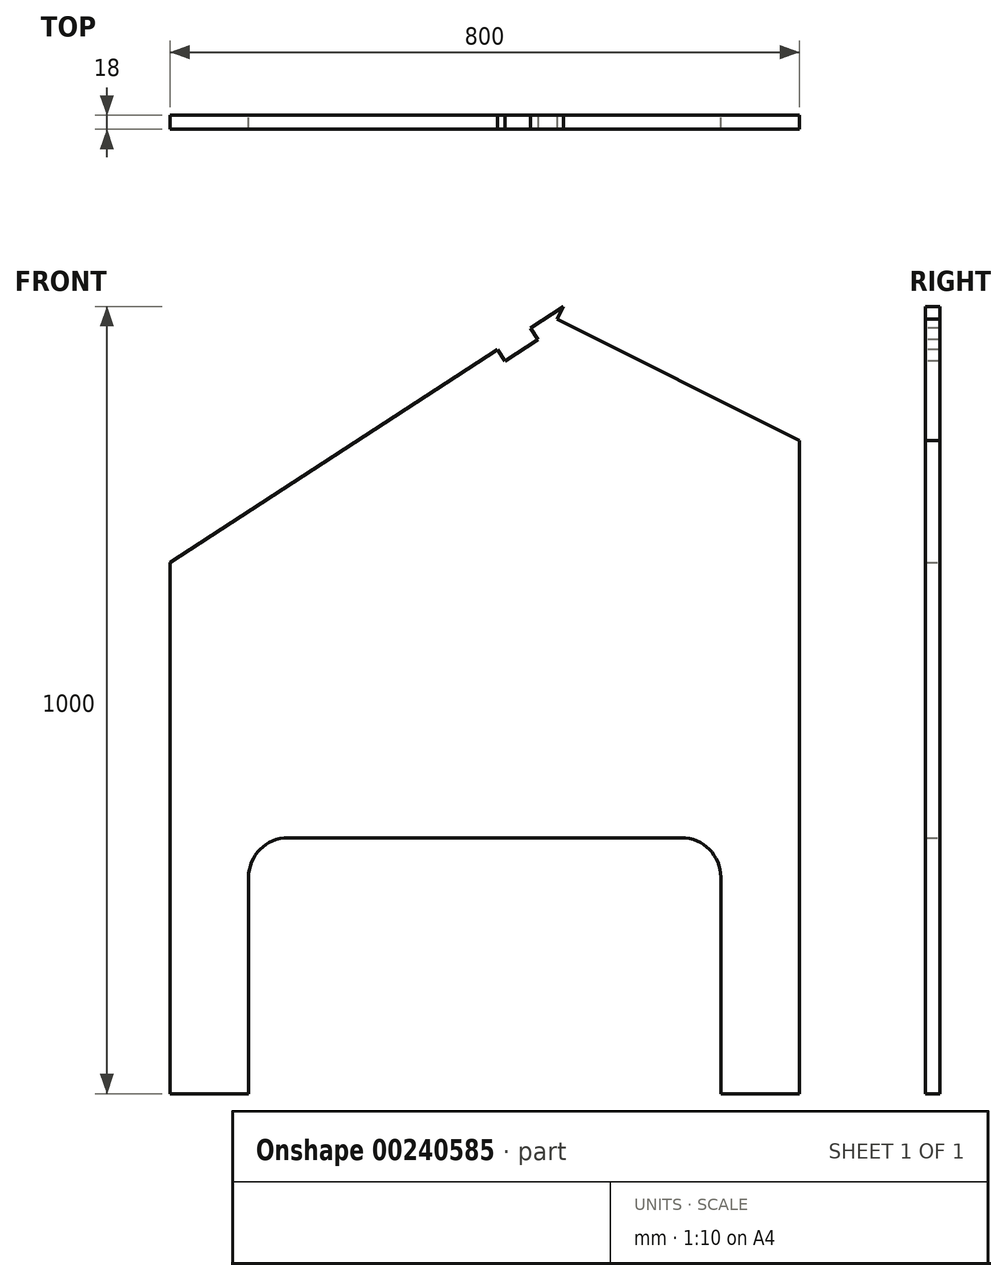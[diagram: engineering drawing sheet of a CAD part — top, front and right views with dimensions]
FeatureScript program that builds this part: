
annotation { "Feature Type Name" : "Feature", "Feature Type Description" : "" }
export const myFeature = defineFeature(function(context is Context, id is Id, definition is map)
    precondition{}
    {
        {
            var Q0;
            Q0=qCreatedBy(makeId("Front.planeOp"),FACE);
            var sketch = newSketch(context, id + "F0", { "sketchPlane" : qUnion([Q0])});
            skLineSegment(sketch, "E0.bottom", {"start": v(0, 0) * mm, "end": v(800, 0) * mm});
            skLineSegment(sketch, "E0.top", {"start": v(0, 1000) * mm, "end": v(800, 1000) * mm});
            skLineSegment(sketch, "E0.left", {"start": v(0, 0) * mm, "end": v(0, 1000) * mm});
            skLineSegment(sketch, "E0.right", {"start": v(800, 0) * mm, "end": v(800, 1000) * mm});
            skLineSegment(sketch, "E1.bottom", {"start": v(100, 0) * mm, "end": v(700, 0) * mm});
            skLineSegment(sketch, "E1.top", {"start": v(150, 325) * mm, "end": v(650, 325) * mm});
            skLineSegment(sketch, "E1.left", {"start": v(100, 0) * mm, "end": v(100, 275) * mm});
            skLineSegment(sketch, "E1.right", {"start": v(700, 0) * mm, "end": v(700, 275) * mm});
            skLineSegment(sketch, "E2", {"start": v(0, 675) * mm, "end": v(500, 1000) * mm});
            skLineSegment(sketch, "E3", {"start": v(500, 1000) * mm, "end": v(800, 850) * mm});
            skPoint(sketch, "E4.visualSharp", {"position": v(100, 325) * mm});
            skArc(sketch, "E4.filletArc", {"start": v(150, 325) * mm, "mid": v(114.64, 310.36) * mm, "end": v(100, 275) * mm});
            skPoint(sketch, "E5.visualSharp", {"position": v(700, 325) * mm});
            skArc(sketch, "E5.filletArc", {"start": v(700, 275) * mm, "mid": v(685.36, 310.36) * mm, "end": v(650, 325) * mm});
            skSolve(sketch);
        }
        {
            var Q0;
            Q0=makeQuery(id+"F0.imprint","IMPRINT",FACE,{"disambiguationData":[TD([[makeQuery(id+"F0.imprint","IMPRINT",EDGE,{"derivedFrom":sQuery(id+"F0.wireOp",EDGE,"E1.top")}),1.0]])]});
            extrude(context, id + "F1", {"entities" : qUnion([Q0]), "depth" : 18 * mm});
        }
        {
            var Q0;
            Q0=makeQuery(id+"F1.opExtrude","CAP_FACE",FACE,{"disambiguationData":[OSD([sQuery(id+"F0.wireOp",EDGE,"E0.bottom"),sQuery(id+"F0.wireOp",EDGE,"E0.left"),sQuery(id+"F0.wireOp",EDGE,"E0.right"),sQuery(id+"F0.wireOp",EDGE,"E1.top"),sQuery(id+"F0.wireOp",EDGE,"E1.left"),sQuery(id+"F0.wireOp",EDGE,"E1.right"),sQuery(id+"F0.wireOp",EDGE,"E2"),sQuery(id+"F0.wireOp",EDGE,"E3"),sQuery(id+"F0.wireOp",EDGE,"E4.filletArc"),sQuery(id+"F0.wireOp",EDGE,"E5.filletArc")])],"isStart":false});
            var sketch = newSketch(context, id + "F2", { "sketchPlane" : qUnion([Q0])});
            skLineSegment(sketch, "E6.0", {"start": v(-6.54, 685.06) * mm, "end": v(493.46, 1010.06) * mm, "construction": true});
            skSolve(sketch);
        }
        {
            var Q0;
            {var subQ2=sQuery(id+"F0.wireOp",EDGE,"E0.left");Q0=makeQuery(id+"F2.imprint","IMPRINT",FACE,{"disambiguationData":[TD([[makeQuery(id+"F2.imprint","IMPRINT",EDGE,{"derivedFrom":makeQuery(id+"F1.opExtrude","CAP_EDGE",EDGE,{"disambiguationData":[OSD([subQ2])],"isStart":false})}),-1.0]])]});}
            var sketch = newSketch(context, id + "F3", { "sketchPlane" : qUnion([Q0])});
            skLineSegment(sketch, "E7", {"start": v(119.23, 766.8) * mm, "end": v(161.15, 794.06) * mm, "construction": true});
            skLineSegment(sketch, "E8", {"start": v(125.77, 756.75) * mm, "end": v(167.69, 784) * mm, "construction": true});
            skLineSegment(sketch, "E9", {"start": v(332.31, 891) * mm, "end": v(374.23, 918.25) * mm, "construction": true});
            skLineSegment(sketch, "E10", {"start": v(332.31, 891) * mm, "end": v(325.77, 901.06) * mm, "construction": true});
            skLineSegment(sketch, "E11", {"start": v(325.77, 901.06) * mm, "end": v(367.7, 928.31) * mm, "construction": true});
            skLineSegment(sketch, "E12", {"start": v(367.7, 928.31) * mm, "end": v(374.23, 918.25) * mm, "construction": true});
            skLineSegment(sketch, "E13", {"start": v(119.23, 766.8) * mm, "end": v(125.77, 756.75) * mm, "construction": true});
            skLineSegment(sketch, "E14", {"start": v(161.15, 794.06) * mm, "end": v(167.69, 784) * mm, "construction": true});
            skLineSegment(sketch, "E15", {"start": v(562.6, 968.7) * mm, "end": v(567.98, 979.43) * mm, "construction": true});
            skLineSegment(sketch, "E16", {"start": v(567.98, 979.43) * mm, "end": v(612.7, 957.07) * mm, "construction": true});
            skLineSegment(sketch, "E17", {"start": v(612.7, 957.07) * mm, "end": v(607.33, 946.33) * mm, "construction": true});
            skLineSegment(sketch, "E18", {"start": v(607.33, 946.33) * mm, "end": v(562.6, 968.7) * mm, "construction": true});
            skLineSegment(sketch, "E19", {"start": v(692.67, 903.67) * mm, "end": v(698.04, 914.4) * mm, "construction": true});
            skLineSegment(sketch, "E20", {"start": v(698.04, 914.4) * mm, "end": v(742.76, 892.04) * mm, "construction": true});
            skLineSegment(sketch, "E21", {"start": v(742.76, 892.04) * mm, "end": v(737.4, 881.3) * mm, "construction": true});
            skLineSegment(sketch, "E22", {"start": v(737.4, 881.3) * mm, "end": v(692.67, 903.67) * mm, "construction": true});
            skSolve(sketch);
        }
        {
            var Q0;
            {var subQ2=sQuery(id+"F0.wireOp",EDGE,"E0.left");Q0=makeQuery(id+"F2.imprint","IMPRINT",FACE,{"disambiguationData":[TD([[makeQuery(id+"F2.imprint","IMPRINT",EDGE,{"derivedFrom":makeQuery(id+"F1.opExtrude","CAP_EDGE",EDGE,{"disambiguationData":[OSD([subQ2])],"isStart":false})}),-1.0]])]});}
            var sketch = newSketch(context, id + "F4", { "sketchPlane" : qUnion([Q0])});
            skLineSegment(sketch, "E23", {"start": v(416.16, 945.5) * mm, "end": v(425.97, 930.4) * mm});
            skLineSegment(sketch, "E24", {"start": v(425.97, 930.4) * mm, "end": v(467.89, 957.66) * mm});
            skLineSegment(sketch, "E25", {"start": v(467.89, 957.66) * mm, "end": v(458.08, 972.75) * mm});
            skLineSegment(sketch, "E26", {"start": v(458.08, 972.75) * mm, "end": v(416.16, 945.5) * mm});
            skSolve(sketch);
        }
        {
            var Q0;
            Q0 = qSketchRegion(id + "F4", true);
            extrude(context, id + "F5", {"entities" : qUnion([Q0]), "operationType" : NewBodyOperationType.REMOVE, "oppositeDirection" : true, "depth" : 18 * mm, "offsetDistance" : 25 * mm});
        }
        {
            var Q0;
            {var subQ2=sQuery(id+"F0.wireOp",EDGE,"E0.left");Q0=makeQuery(id+"F2.imprint","IMPRINT",FACE,{"disambiguationData":[TD([[makeQuery(id+"F2.imprint","IMPRINT",EDGE,{"derivedFrom":makeQuery(id+"F1.opExtrude","CAP_EDGE",EDGE,{"disambiguationData":[OSD([subQ2])],"isStart":false})}),-1.0]])]});}
            var sketch = newSketch(context, id + "F6", { "sketchPlane" : qUnion([Q0])});
            skLineSegment(sketch, "E27", {"start": v(491.95, 983.9) * mm, "end": v(500, 1000) * mm});
            skLineSegment(sketch, "E28", {"start": v(500, 1000) * mm, "end": v(857.77, 821.11) * mm});
            skLineSegment(sketch, "E29", {"start": v(857.77, 821.11) * mm, "end": v(849.72, 805.01) * mm});
            skLineSegment(sketch, "E30", {"start": v(849.72, 805.01) * mm, "end": v(491.95, 983.9) * mm});
            skSolve(sketch);
        }
        {
            var Q0;
            Q0 = qSketchRegion(id + "F6", true);
            extrude(context, id + "F7", {"entities" : qUnion([Q0]), "operationType" : NewBodyOperationType.REMOVE, "endBound" : BoundingType.UP_TO_NEXT, "oppositeDirection" : true, "depth" : 25 * mm, "offsetDistance" : 25 * mm});
        }
    });
